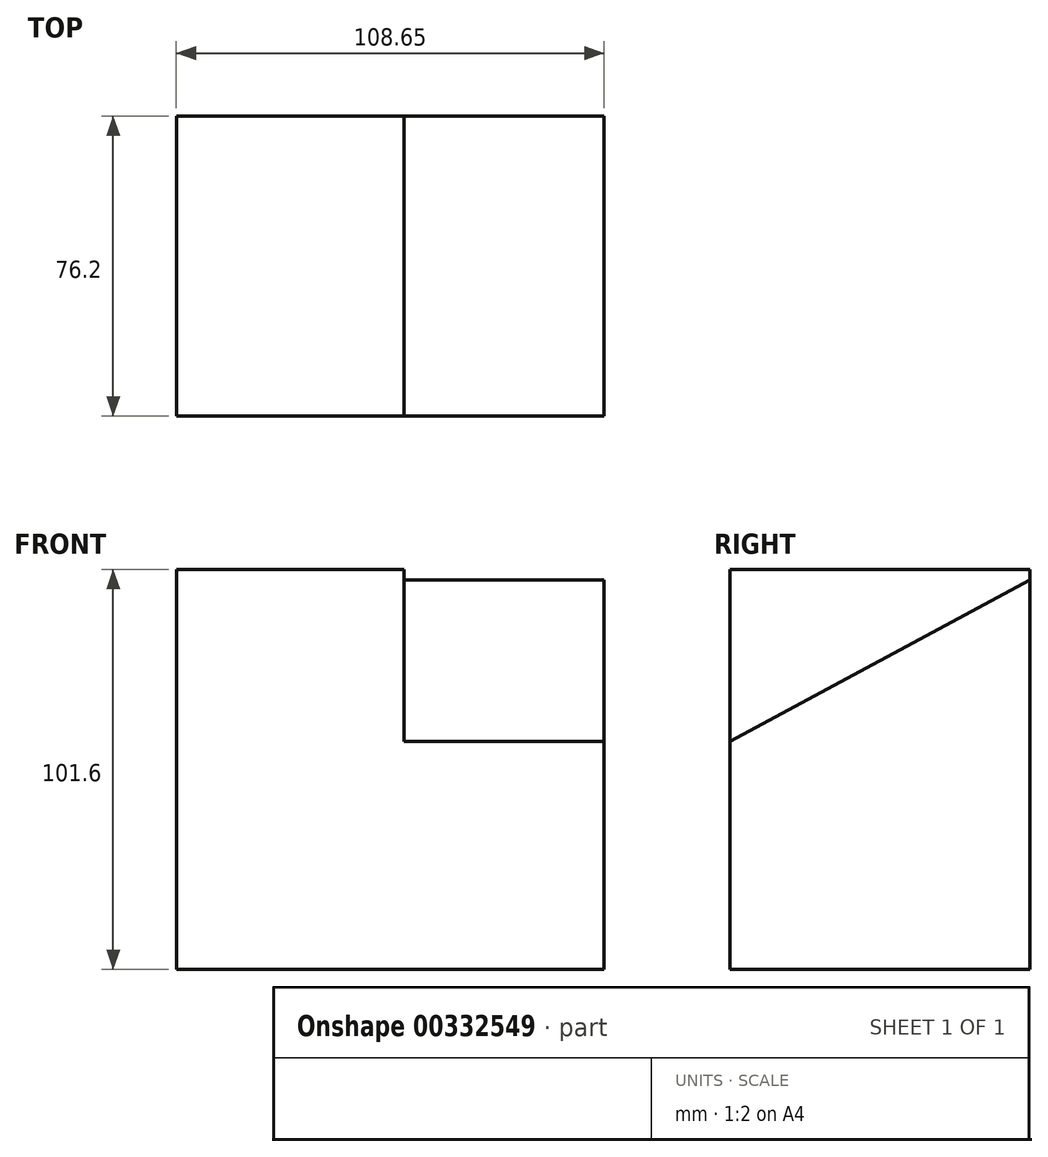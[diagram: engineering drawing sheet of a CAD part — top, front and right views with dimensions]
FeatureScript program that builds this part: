
annotation { "Feature Type Name" : "Feature", "Feature Type Description" : "" }
export const myFeature = defineFeature(function(context is Context, id is Id, definition is map)
    precondition{}
    {
        {
            var Q0;
            Q0=qCreatedBy(makeId("Front.planeOp"),FACE);
            var sketch = newSketch(context, id + "F0", { "sketchPlane" : qUnion([Q0])});
            skLineSegment(sketch, "E0.bottom", {"start": v(-51.54, 43.68) * mm, "end": v(57.1, 43.68) * mm});
            skLineSegment(sketch, "E0.top", {"start": v(-51.54, -57.92) * mm, "end": v(57.1, -57.92) * mm});
            skLineSegment(sketch, "E0.left", {"start": v(-51.54, 43.68) * mm, "end": v(-51.54, -57.92) * mm});
            skLineSegment(sketch, "E0.right", {"start": v(57.1, 43.68) * mm, "end": v(57.1, -57.92) * mm});
            skSolve(sketch);
        }
        {
            var Q0;
            Q0=makeQuery(id+"F0.imprint","IMPRINT",FACE,{"disambiguationData":[TD([[makeQuery(id+"F0.imprint","IMPRINT",EDGE,{"derivedFrom":sQuery(id+"F0.wireOp",EDGE,"E0.bottom")}),-1.0]])]});
            extrude(context, id + "F1", {"entities" : qUnion([Q0]), "depth" : 76.2 * mm});
        }
        {
            var Q0;
            Q0=makeQuery(id+"F1.opExtrude","SWEPT_FACE",FACE,{"disambiguationData":[OSD([sQuery(id+"F0.wireOp",EDGE,"E0.right")])]});
            var sketch = newSketch(context, id + "F2", { "sketchPlane" : qUnion([Q0])});
            skLineSegment(sketch, "E1", {"start": v(-76.2, 43.68) * mm, "end": v(-76.2, 0) * mm});
            skLineSegment(sketch, "E2", {"start": v(-76.2, 0) * mm, "end": v(0, 0) * mm});
            skLineSegment(sketch, "E3", {"start": v(0, 0) * mm, "end": v(0, 43.68) * mm});
            skLineSegment(sketch, "E4", {"start": v(0, 43.68) * mm, "end": v(-76.2, 43.68) * mm});
            skSolve(sketch);
        }
        {
            var Q0;
            Q0=makeQuery(id+"F2.imprint","IMPRINT",FACE,{"disambiguationData":[TD([[makeQuery(id+"F2.imprint","IMPRINT",EDGE,{"derivedFrom":sQuery(id+"F2.wireOp",EDGE,"E1")}),1.0]])]});
            extrude(context, id + "F3", {"entities" : qUnion([Q0]), "operationType" : NewBodyOperationType.REMOVE, "oppositeDirection" : true, "depth" : 50.8 * mm});
        }
        {
            var Q0;
            Q0=makeQuery(id+"F3.boolean.opBoolean","COPY",FACE,{"derivedFrom":makeQuery(id+"F3.opExtrude","CAP_FACE",FACE,{"disambiguationData":[OSD([sQuery(id+"F2.wireOp",EDGE,"E1"),sQuery(id+"F2.wireOp",EDGE,"E2"),sQuery(id+"F2.wireOp",EDGE,"E3"),sQuery(id+"F2.wireOp",EDGE,"E4")])],"isStart":false})});
            var sketch = newSketch(context, id + "F4", { "sketchPlane" : qUnion([Q0])});
            skLineSegment(sketch, "E5", {"start": v(0, 41.01) * mm, "end": v(-76.2, 0) * mm});
            skLineSegment(sketch, "E6", {"start": v(-76.2, 0) * mm, "end": v(0, 0) * mm});
            skLineSegment(sketch, "E7", {"start": v(0, 0) * mm, "end": v(0, 41.01) * mm});
            skSolve(sketch);
        }
        {
            var Q0;
            Q0=makeQuery(id+"F4.imprint","IMPRINT",FACE,{"disambiguationData":[TD([[makeQuery(id+"F4.imprint","IMPRINT",EDGE,{"derivedFrom":sQuery(id+"F4.wireOp",EDGE,"E5")}),1.0]])]});
            extrude(context, id + "F5", {"entities" : qUnion([Q0]), "operationType" : NewBodyOperationType.ADD, "depth" : 50.8 * mm});
        }
    });
